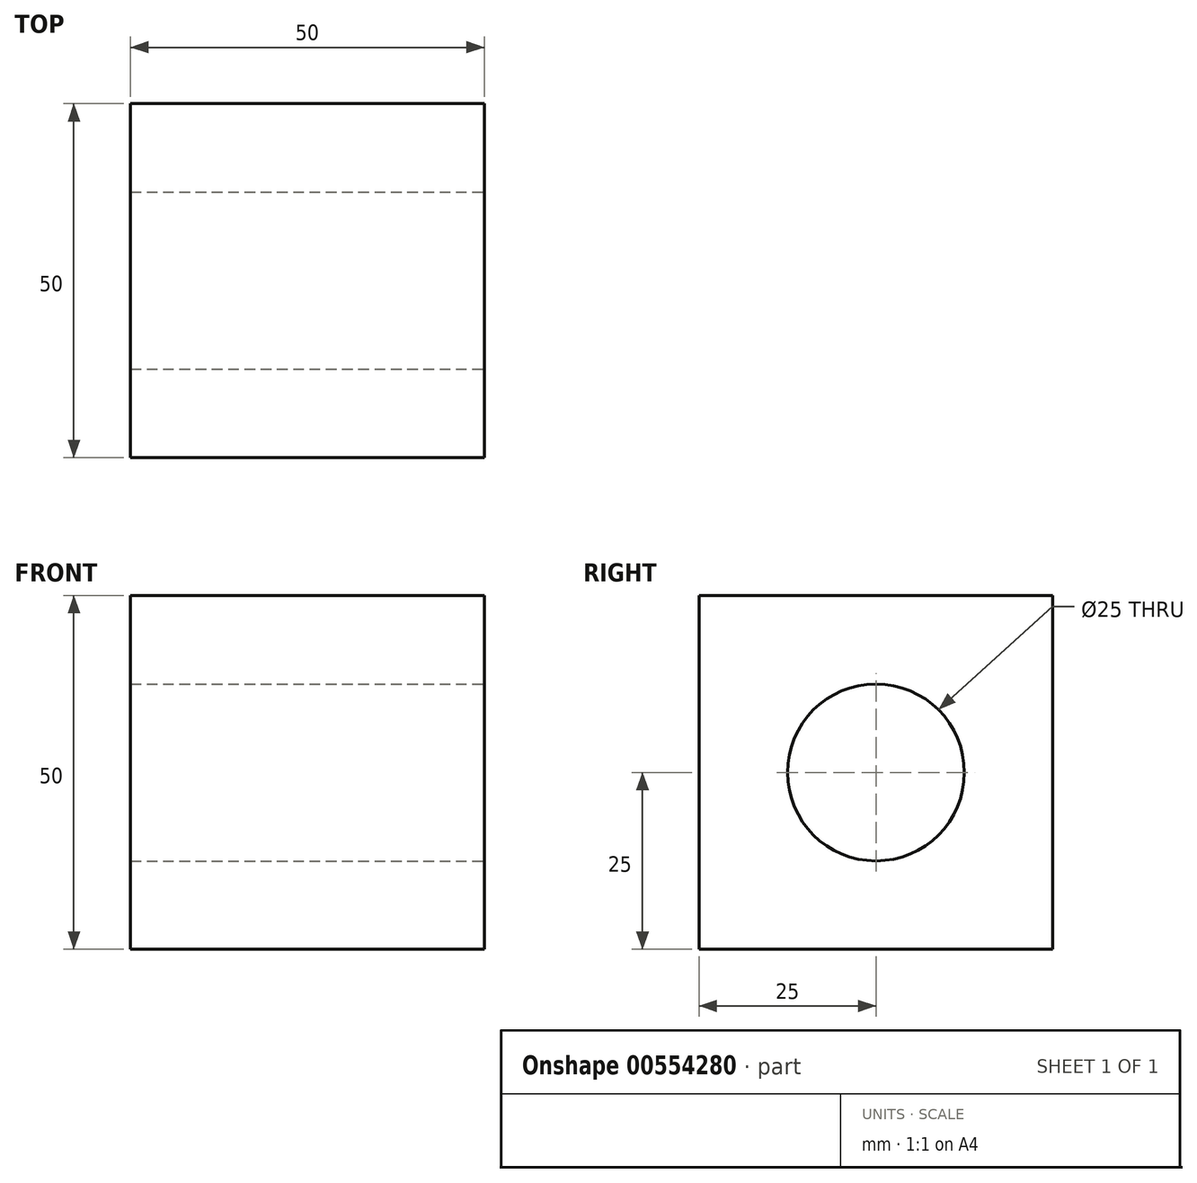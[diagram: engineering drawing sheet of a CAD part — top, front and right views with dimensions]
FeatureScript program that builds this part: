
annotation { "Feature Type Name" : "Feature", "Feature Type Description" : "" }
export const myFeature = defineFeature(function(context is Context, id is Id, definition is map)
    precondition{}
    {
        {
            var Q0;
            Q0=qCreatedBy(makeId("Top.planeOp"),FACE);
            var sketch = newSketch(context, id + "F0", { "sketchPlane" : qUnion([Q0])});
            skLineSegment(sketch, "E0.bottom", {"start": v(0, 50) * mm, "end": v(50, 50) * mm});
            skLineSegment(sketch, "E0.top", {"start": v(0, 0) * mm, "end": v(50, 0) * mm});
            skLineSegment(sketch, "E0.left", {"start": v(0, 50) * mm, "end": v(0, 0) * mm});
            skLineSegment(sketch, "E0.right", {"start": v(50, 50) * mm, "end": v(50, 0) * mm});
            skSolve(sketch);
        }
        {
            var Q0;
            Q0 = qSketchRegion(id + "F0", true);
            extrude(context, id + "F1", {"entities" : qUnion([Q0]), "depth" : 50 * mm, "offsetDistance" : 25 * mm});
        }
        {
            var Q0;
            Q0=makeQuery(id+"F1.opExtrude","SWEPT_FACE",FACE,{"disambiguationData":[OSD([sQuery(id+"F0.wireOp",EDGE,"E0.right")])]});
            var sketch = newSketch(context, id + "F2", { "sketchPlane" : qUnion([Q0])});
            skCircle(sketch, "E1", {"center": v(25, 25) * mm, "radius": 12.5 * mm});
            skSolve(sketch);
        }
        {
            var Q0;
            Q0 = qSketchRegion(id + "F2", true);
            extrude(context, id + "F3", {"entities" : qUnion([Q0]), "operationType" : NewBodyOperationType.REMOVE, "oppositeDirection" : true, "depth" : 50 * mm, "offsetDistance" : 25 * mm});
        }
    });
